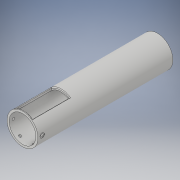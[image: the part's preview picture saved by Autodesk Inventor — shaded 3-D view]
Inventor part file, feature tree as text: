
AUTODESK INVENTOR PART (.ipt)
format: ipt  version: 2019 (Build 230136000, 136)  size: 164,352 bytes
history: native  units: mm
features: other x4, sketch x3, extrude x1, hole x1, pattern_circular x1, chamfer x1
ambient origin geometry x8: Origin, YZ Plane, XZ Plane, XY Plane, X Axis, Y Axis, Z Axis, Center Point
bodies: Solide1 (feature_tree)
feature tree (11):
  other  "Révolution1"
  extrude  "Extrusion2"  Depth=38.0mm
  other  "Plan de construction2"
  hole  "Perçage1"  [1 undecoded]
  pattern_circular  "Réseau circulaire2"  Angle=90.0deg  [1 undecoded]
  chamfer  "Chanfrein2"  Distance=100.0mm
  other  "Plan de construction3"
  other  "Filetage3"
  sketch  "Esquisse1"
  sketch  "Esquisse3"
  sketch  "Esquisse4"
note: 2 required parameter values undecoded (feature->parameter linkage not recoverable at this tier; creation-order binding heuristic only, values carry confidence <= 0.55)
